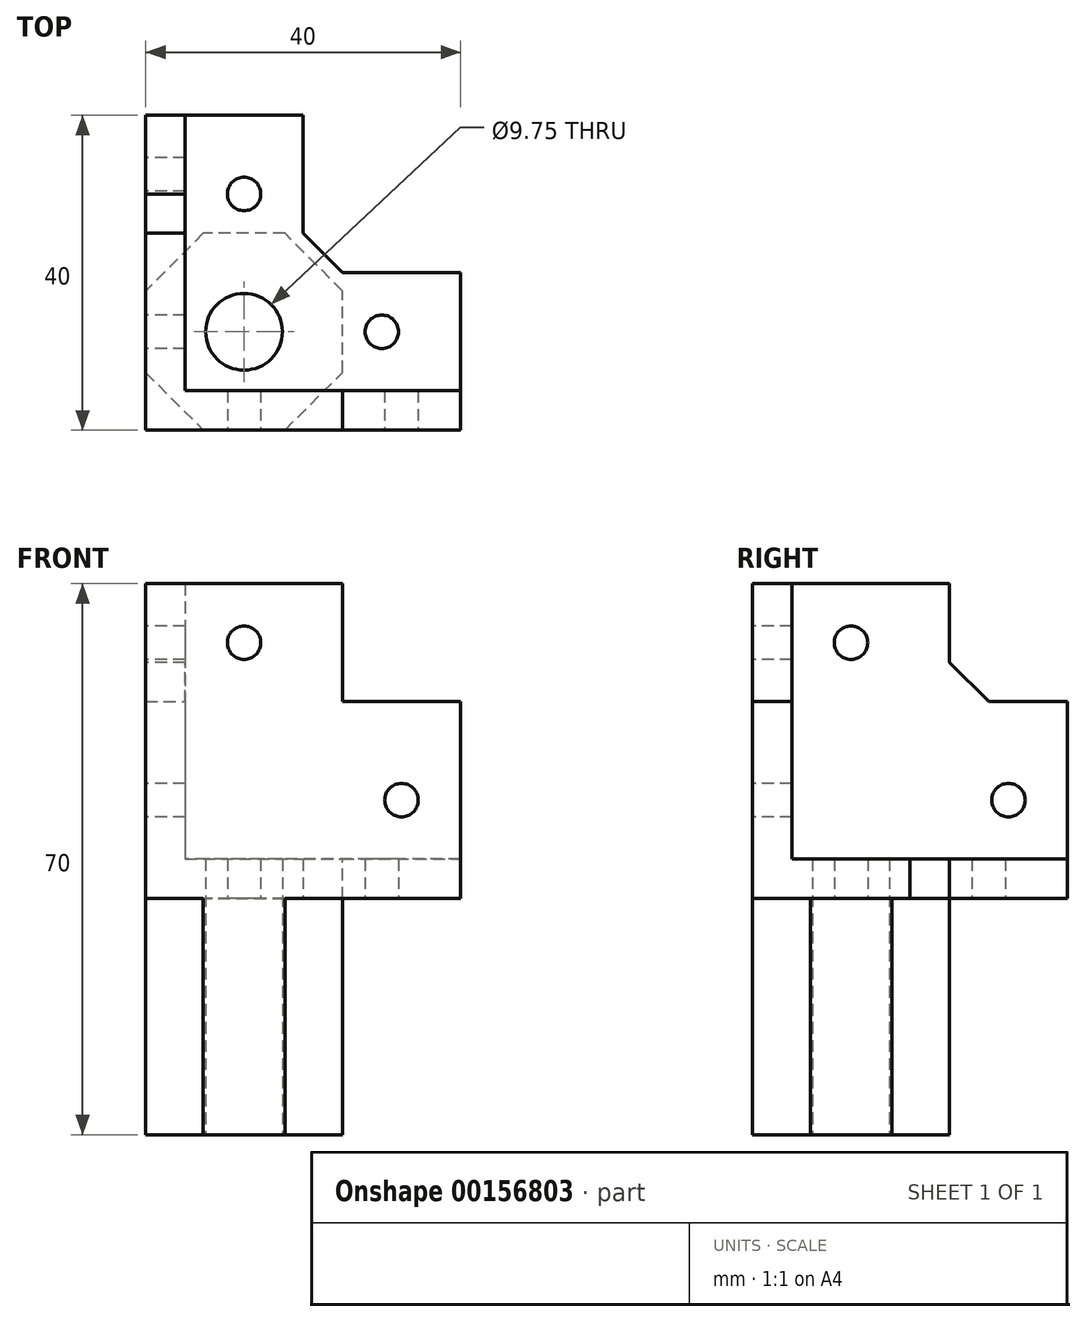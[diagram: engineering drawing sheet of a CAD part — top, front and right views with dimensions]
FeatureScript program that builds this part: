
annotation { "Feature Type Name" : "Feature", "Feature Type Description" : "" }
export const myFeature = defineFeature(function(context is Context, id is Id, definition is map)
    precondition{}
    {
        {
            var Q0;
            Q0=qCreatedBy(makeId("Top.planeOp"),FACE);
            var sketch = newSketch(context, id + "F0", { "sketchPlane" : qUnion([Q0])});
            skCircle(sketch, "E0", {"center": v(0, 0) * mm, "radius": 4.88 * mm});
            skLineSegment(sketch, "E1", {"start": v(-12.5, 0) * mm, "end": v(-12.5, 27.5) * mm});
            skLineSegment(sketch, "E2", {"start": v(-12.5, 27.5) * mm, "end": v(7.5, 27.5) * mm});
            skLineSegment(sketch, "E3", {"start": v(7.5, 27.5) * mm, "end": v(7.5, 7.5) * mm});
            skLineSegment(sketch, "E4", {"start": v(7.5, 7.5) * mm, "end": v(27.5, 7.5) * mm});
            skLineSegment(sketch, "E5", {"start": v(27.5, 7.5) * mm, "end": v(27.5, -12.5) * mm});
            skLineSegment(sketch, "E6", {"start": v(27.5, -12.5) * mm, "end": v(-12.5, -12.5) * mm});
            skLineSegment(sketch, "E7", {"start": v(-12.5, -12.5) * mm, "end": v(-12.5, 0) * mm});
            skCircle(sketch, "E8", {"center": v(0, 17.5) * mm, "radius": 2.12 * mm});
            skCircle(sketch, "E9", {"center": v(17.5, 0) * mm, "radius": 2.12 * mm});
            skPoint(sketch, "E10.visualSharp", {"position": v(-12.5, -12.5) * mm});
            skLineSegment(sketch, "E10.filletArc", {"start": v(-12.5, -12.5) * mm, "end": v(-12.5, -12.5) * mm});
            skSolve(sketch);
        }
        {
            var Q0;
            Q0=qSketchRegion(id+"F0",true);
            extrude(context, id + "F1", {"entities" : qUnion([Q0]), "depth" : 5 * mm});
        }
        {
            var Q0;
            Q0=makeQuery(id+"F1.opExtrude","CAP_FACE",FACE,{"disambiguationData":[OSD([sQuery(id+"F0.wireOp",EDGE,"E0"),sQuery(id+"F0.wireOp",EDGE,"E1"),sQuery(id+"F0.wireOp",EDGE,"E2"),sQuery(id+"F0.wireOp",EDGE,"E3"),sQuery(id+"F0.wireOp",EDGE,"E4"),sQuery(id+"F0.wireOp",EDGE,"E5"),sQuery(id+"F0.wireOp",EDGE,"E6"),sQuery(id+"F0.wireOp",EDGE,"E7"),sQuery(id+"F0.wireOp",EDGE,"E8"),sQuery(id+"F0.wireOp",EDGE,"E9"),sQuery(id+"F0.wireOp",EDGE,"E10.filletArc")])],"isStart":true});
            var sketch = newSketch(context, id + "F2", { "sketchPlane" : qUnion([Q0])});
            skCircle(sketch, "E11.cCircle", {"center": v(0, 0) * mm, "radius": 12.5 * mm, "construction": true});
            skLineSegment(sketch, "E11.0", {"start": v(12.5, 5.18) * mm, "end": v(12.5, -5.18) * mm});
            skLineSegment(sketch, "E11.1", {"start": v(12.5, -5.18) * mm, "end": v(5.18, -12.5) * mm});
            skLineSegment(sketch, "E11.2", {"start": v(5.18, -12.5) * mm, "end": v(-5.18, -12.5) * mm});
            skLineSegment(sketch, "E11.3", {"start": v(-5.18, -12.5) * mm, "end": v(-12.5, -5.18) * mm});
            skLineSegment(sketch, "E11.4", {"start": v(-12.5, -5.18) * mm, "end": v(-12.5, 5.18) * mm});
            skLineSegment(sketch, "E11.5", {"start": v(-12.5, 5.18) * mm, "end": v(-5.18, 12.5) * mm});
            skLineSegment(sketch, "E11.6", {"start": v(-5.18, 12.5) * mm, "end": v(5.18, 12.5) * mm});
            skLineSegment(sketch, "E11.7", {"start": v(5.18, 12.5) * mm, "end": v(12.5, 5.18) * mm});
            skPoint(sketch, "E11.0.midPoint", {"position": v(12.5, 0) * mm});
            skCircle(sketch, "E12", {"center": v(0, 0) * mm, "radius": 4.88 * mm});
            skLineSegment(sketch, "E13", {"start": v(7.5, -7.5) * mm, "end": v(7.5, -10.18) * mm});
            skLineSegment(sketch, "E14", {"start": v(7.5, -7.5) * mm, "end": v(10.18, -7.5) * mm});
            skSolve(sketch);
        }
        {
            var Q0;
            Q0=qSketchRegion(id+"F2",true);
            extrude(context, id + "F3", {"entities" : qUnion([Q0]), "operationType" : NewBodyOperationType.ADD, "depth" : 30 * mm});
        }
        {
            var Q0;
            Q0=makeQuery(id+"F1.opExtrude","SWEPT_EDGE",EDGE,{"disambiguationData":[OSD([sQuery(id+"F0.wireOp",EDGE,"E3"),sQuery(id+"F0.wireOp",EDGE,"E4")])]});
            chamfer(context, id + "F4", {"entities" : qUnion([Q0]), "width" : 5 * mm, "tangentPropagation" : true});
        }
        {
            var Q0;
            Q0=makeQuery(id+"F1.opExtrude","CAP_FACE",FACE,{"disambiguationData":[OSD([sQuery(id+"F0.wireOp",EDGE,"E0"),sQuery(id+"F0.wireOp",EDGE,"E1"),sQuery(id+"F0.wireOp",EDGE,"E2"),sQuery(id+"F0.wireOp",EDGE,"E3"),sQuery(id+"F0.wireOp",EDGE,"E4"),sQuery(id+"F0.wireOp",EDGE,"E5"),sQuery(id+"F0.wireOp",EDGE,"E6"),sQuery(id+"F0.wireOp",EDGE,"E7"),sQuery(id+"F0.wireOp",EDGE,"E8"),sQuery(id+"F0.wireOp",EDGE,"E9")])],"isStart":false});
            var sketch = newSketch(context, id + "F5", { "sketchPlane" : qUnion([Q0])});
            skLineSegment(sketch, "E15", {"start": v(-12.5, 27.5) * mm, "end": v(-12.5, -12.5) * mm});
            skLineSegment(sketch, "E16", {"start": v(-12.5, -12.5) * mm, "end": v(27.5, -12.5) * mm});
            skLineSegment(sketch, "E17", {"start": v(27.5, -12.5) * mm, "end": v(27.5, -7.5) * mm});
            skLineSegment(sketch, "E18", {"start": v(27.5, -7.5) * mm, "end": v(-7.5, -7.5) * mm});
            skLineSegment(sketch, "E19", {"start": v(-7.5, -7.5) * mm, "end": v(-7.5, 27.5) * mm});
            skLineSegment(sketch, "E20", {"start": v(-7.5, 27.5) * mm, "end": v(-12.5, 27.5) * mm});
            skSolve(sketch);
        }
        {
            var Q0;
            Q0=qSketchRegion(id+"F5",true);
            extrude(context, id + "F6", {"entities" : qUnion([Q0]), "operationType" : NewBodyOperationType.ADD, "depth" : 20 * mm});
        }
        {
            var Q0;
            Q0=makeQuery(id+"F6.opExtrude","CAP_FACE",FACE,{"disambiguationData":[OSD([sQuery(id+"F5.wireOp",EDGE,"E15"),sQuery(id+"F5.wireOp",EDGE,"E16"),sQuery(id+"F5.wireOp",EDGE,"E17"),sQuery(id+"F5.wireOp",EDGE,"E18"),sQuery(id+"F5.wireOp",EDGE,"E19"),sQuery(id+"F5.wireOp",EDGE,"E20")])],"isStart":false});
            var sketch = newSketch(context, id + "F7", { "sketchPlane" : qUnion([Q0])});
            skLineSegment(sketch, "E21", {"start": v(-12.5, 12.5) * mm, "end": v(-12.5, -12.5) * mm});
            skLineSegment(sketch, "E22", {"start": v(-12.5, -12.5) * mm, "end": v(12.5, -12.5) * mm});
            skLineSegment(sketch, "E23", {"start": v(12.5, -12.5) * mm, "end": v(12.5, -7.5) * mm});
            skLineSegment(sketch, "E24", {"start": v(12.5, -7.5) * mm, "end": v(-7.5, -7.5) * mm});
            skLineSegment(sketch, "E25", {"start": v(-7.5, -7.5) * mm, "end": v(-7.5, 12.5) * mm});
            skLineSegment(sketch, "E26", {"start": v(-7.5, 12.5) * mm, "end": v(-12.5, 12.5) * mm});
            skSolve(sketch);
        }
        {
            var Q0;
            Q0=qSketchRegion(id+"F7",true);
            extrude(context, id + "F8", {"entities" : qUnion([Q0]), "operationType" : NewBodyOperationType.ADD, "depth" : 15 * mm});
        }
        {
            var Q0;
            Q0=makeQuery(id+"F8.boolean.opBoolean","MERGE",FACE,{"derivedFrom":[makeQuery(id+"F6.boolean.opBoolean","MERGE",FACE,{"derivedFrom":[makeQuery(id+"F3.boolean.opBoolean","MERGE",FACE,{"derivedFrom":[makeQuery(id+"F1.opExtrude","SWEPT_FACE",FACE,{"disambiguationData":[OSD([sQuery(id+"F0.wireOp",EDGE,"E6")])]}),makeQuery(id+"F3.opExtrude","SWEPT_FACE",FACE,{"disambiguationData":[OSD([sQuery(id+"F2.wireOp",EDGE,"E11.6")])]})]}),makeQuery(id+"F6.opExtrude","SWEPT_FACE",FACE,{"disambiguationData":[OSD([sQuery(id+"F5.wireOp",EDGE,"E16")])]})]}),makeQuery(id+"F8.opExtrude","SWEPT_FACE",FACE,{"disambiguationData":[OSD([sQuery(id+"F7.wireOp",EDGE,"E22")])]})]});
            var sketch = newSketch(context, id + "F9", { "sketchPlane" : qUnion([Q0])});
            skCircle(sketch, "E27", {"center": v(20, 12.5) * mm, "radius": 2.12 * mm});
            skCircle(sketch, "E28", {"center": v(0, 32.5) * mm, "radius": 2.12 * mm});
            skSolve(sketch);
        }
        {
            var Q0;
            Q0=qSketchRegion(id+"F9",true);
            extrude(context, id + "F10", {"entities" : qUnion([Q0]), "operationType" : NewBodyOperationType.REMOVE, "endBound" : BoundingType.THROUGH_ALL, "oppositeDirection" : true, "depth" : 25 * mm});
        }
        {
            var Q0;
            Q0=makeQuery(id+"F8.boolean.opBoolean","MERGE",FACE,{"derivedFrom":[makeQuery(id+"F6.boolean.opBoolean","MERGE",FACE,{"derivedFrom":[makeQuery(id+"F3.boolean.opBoolean","MERGE",FACE,{"derivedFrom":[makeQuery(id+"F1.opExtrude","SWEPT_FACE",FACE,{"disambiguationData":[OSD([sQuery(id+"F0.wireOp",EDGE,"E1"),sQuery(id+"F0.wireOp",EDGE,"E7")])]}),makeQuery(id+"F3.opExtrude","SWEPT_FACE",FACE,{"disambiguationData":[OSD([sQuery(id+"F2.wireOp",EDGE,"E11.4")])]})]}),makeQuery(id+"F6.opExtrude","SWEPT_FACE",FACE,{"disambiguationData":[OSD([sQuery(id+"F5.wireOp",EDGE,"E15")])]})]}),makeQuery(id+"F8.opExtrude","SWEPT_FACE",FACE,{"disambiguationData":[OSD([sQuery(id+"F7.wireOp",EDGE,"E21")])]})]});
            var sketch = newSketch(context, id + "F11", { "sketchPlane" : qUnion([Q0])});
            skCircle(sketch, "E29", {"center": v(-20, 12.5) * mm, "radius": 2.12 * mm});
            skCircle(sketch, "E30", {"center": v(0, 32.5) * mm, "radius": 2.12 * mm});
            skSolve(sketch);
        }
        {
            var Q0;
            Q0=qSketchRegion(id+"F11",true);
            extrude(context, id + "F12", {"entities" : qUnion([Q0]), "operationType" : NewBodyOperationType.REMOVE, "endBound" : BoundingType.THROUGH_ALL, "oppositeDirection" : true, "depth" : 25 * mm});
        }
        {
            var Q0;
            Q0=makeQuery(id+"F8.opExtrude","CAP_EDGE",EDGE,{"disambiguationData":[OSD([sQuery(id+"F7.wireOp",EDGE,"E23")])],"isStart":true});
            var Q1;
            Q1=makeQuery(id+"F8.opExtrude","CAP_EDGE",EDGE,{"disambiguationData":[OSD([sQuery(id+"F7.wireOp",EDGE,"E26")])],"isStart":true});
            chamfer(context, id + "F13", {"entities" : qUnion([Q0, Q1]), "width" : 5 * mm, "tangentPropagation" : true});
        }
    });
